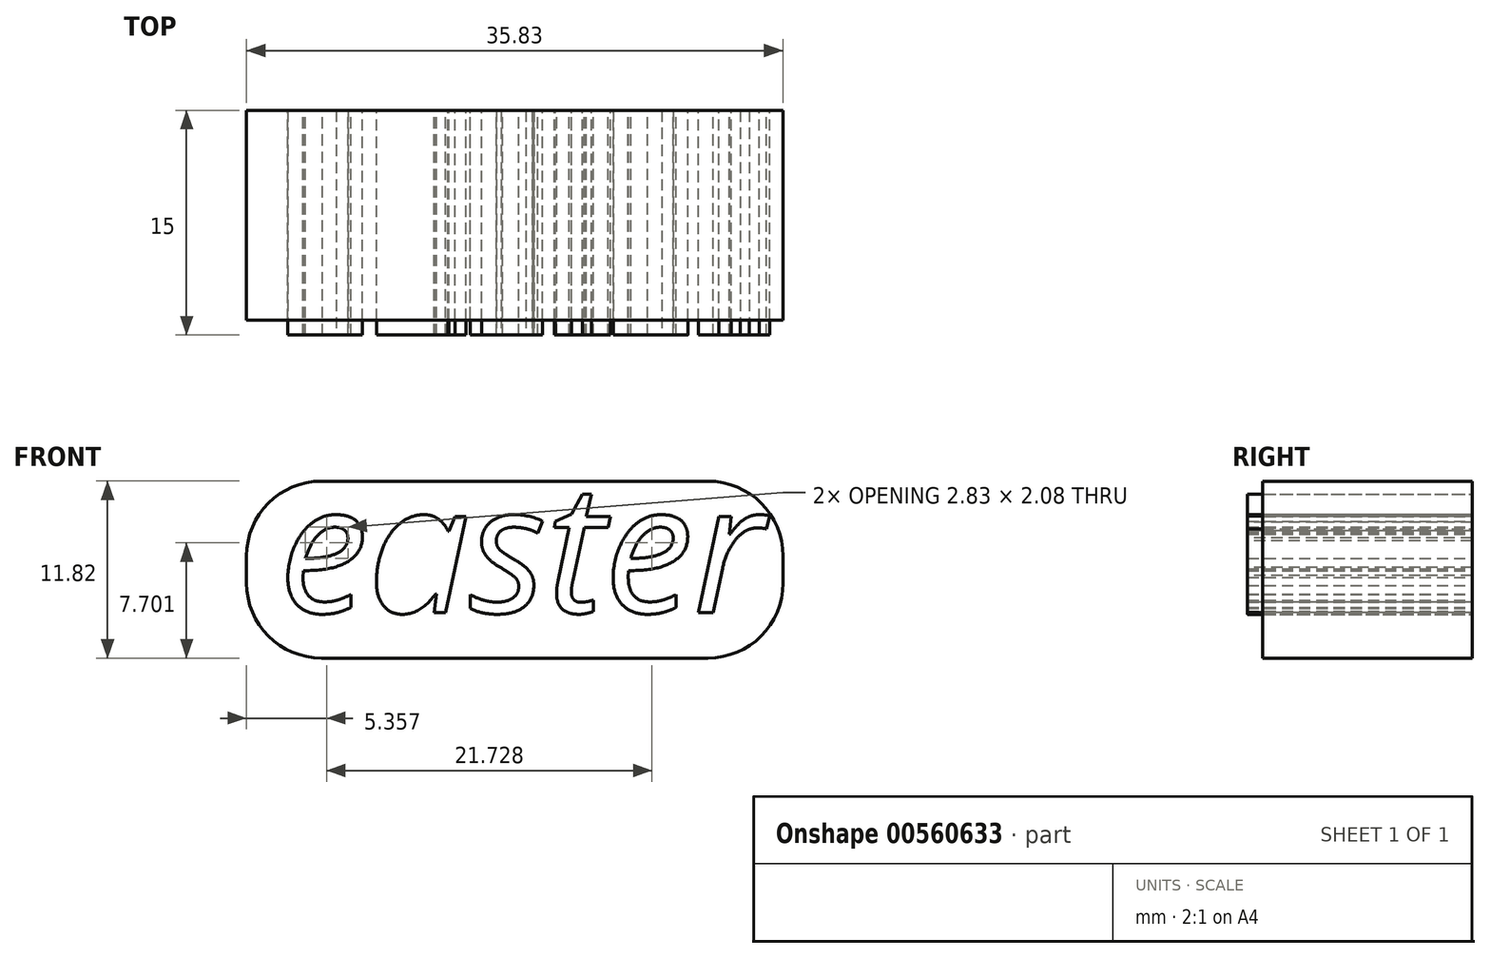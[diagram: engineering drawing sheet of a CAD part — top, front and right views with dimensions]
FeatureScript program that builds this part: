
annotation { "Feature Type Name" : "Feature", "Feature Type Description" : "" }
export const myFeature = defineFeature(function(context is Context, id is Id, definition is map)
    precondition{}
    {
        {
            var Q0;
            Q0=qCreatedBy(makeId("Front.planeOp"),FACE);
            var sketch = newSketch(context, id + "F0", { "sketchPlane" : qUnion([Q0])});
            skPoint(sketch, "E0.21.internal.orphan", {"position": v(0, -2.46) * mm});
            skPoint(sketch, "E0.22.internal.orphan", {"position": v(0, -2.08) * mm});
            skPoint(sketch, "E0.28.internal.orphan", {"position": v(-2.91, 0) * mm});
            skPoint(sketch, "E0.7.internal.orphan", {"position": v(0, 5.92) * mm});
            skText(sketch, "E1", { "text": "easter\n", "fontName": "OpenSans-Italic.ttf"});
            skLineSegment(sketch, "E2.bottom", {"start": v(-20.06, 30.88) * mm, "end": v(19.94, 30.88) * mm, "construction": true});
            skLineSegment(sketch, "E2.top", {"start": v(-20.06, -9.12) * mm, "end": v(19.94, -9.12) * mm, "construction": true});
            skLineSegment(sketch, "E2.left", {"start": v(-20.06, 30.88) * mm, "end": v(-20.06, -9.12) * mm, "construction": true});
            skLineSegment(sketch, "E2.right", {"start": v(19.94, 30.88) * mm, "end": v(19.94, -9.12) * mm, "construction": true});
            const initialGuessF0  = {"E1": [-0.0168, -0.00387, 1, 0, 0.00864]};
            skSetInitialGuess(sketch, initialGuessF0);
            skSolve(sketch);
        }
        {
            var Q0;
            Q0 = qSketchRegion(id + "F0", true);
            var Q1;
            Q1=makeQuery(id+"F0.imprint","IMPRINT",FACE,{"disambiguationData":[TD([[makeQuery(id+"F0.imprint","IMPRINT",EDGE,{"derivedFrom":sQuery(id+"F0.wireOp",EDGE,"E1.sketch_text.stroke-40")}),1.0]])]});
            extrude(context, id + "F1", {"entities" : qUnion([Q0, Q1]), "depth" : 15 * mm, "offsetDistance" : 25 * mm});
        }
        {
            var Q0;
            Q0=qCreatedBy(makeId("Front.planeOp"),FACE);
            var sketch = newSketch(context, id + "F2", { "sketchPlane" : qUnion([Q0])});
            skLineSegment(sketch, "E3.bottom", {"start": v(-13.99, 4.9) * mm, "end": v(11.84, 4.9) * mm});
            skLineSegment(sketch, "E3.top", {"start": v(-13.99, -6.9) * mm, "end": v(11.84, -6.9) * mm});
            skLineSegment(sketch, "E3.left", {"start": v(-18.99, -0.1) * mm, "end": v(-18.99, -1.9) * mm});
            skLineSegment(sketch, "E3.right", {"start": v(16.84, -0.1) * mm, "end": v(16.84, -1.9) * mm});
            skPoint(sketch, "E4.visualSharp", {"position": v(-18.99, 4.9) * mm});
            skPoint(sketch, "E5.visualSharp", {"position": v(16.84, 4.9) * mm});
            skPoint(sketch, "E6.visualSharp", {"position": v(16.84, -6.9) * mm});
            skPoint(sketch, "E7.visualSharp", {"position": v(-18.99, -6.9) * mm});
            skLineSegment(sketch, "E8", {"start": v(-18.99, -6.9) * mm, "end": v(-18.99, -8.23) * mm});
            skLineSegment(sketch, "E9", {"start": v(-17.4, -9.82) * mm, "end": v(-18.99, -6.9) * mm});
            skLineSegment(sketch, "E10", {"start": v(15.26, -9.82) * mm, "end": v(16.84, -6.9) * mm});
            skLineSegment(sketch, "E11", {"start": v(16.84, -6.9) * mm, "end": v(16.84, -8.23) * mm});
            skLineSegment(sketch, "E12", {"start": v(16.84, 3.33) * mm, "end": v(16.84, 4.9) * mm});
            skLineSegment(sketch, "E13", {"start": v(15.26, 4.9) * mm, "end": v(16.84, 4.9) * mm});
            skLineSegment(sketch, "E14", {"start": v(-18.99, 4.9) * mm, "end": v(-18.99, 3.33) * mm});
            skLineSegment(sketch, "E15", {"start": v(-17.4, 4.9) * mm, "end": v(-18.99, 4.9) * mm});
            skLineSegment(sketch, "E16.bottom", {"start": v(-20.68, 23.25) * mm, "end": v(19.32, 23.25) * mm, "construction": true});
            skLineSegment(sketch, "E16.top", {"start": v(-20.68, -16.75) * mm, "end": v(19.32, -16.75) * mm, "construction": true});
            skLineSegment(sketch, "E16.left", {"start": v(-20.68, 23.25) * mm, "end": v(-20.68, -16.75) * mm, "construction": true});
            skLineSegment(sketch, "E16.right", {"start": v(19.32, 23.25) * mm, "end": v(19.32, -16.75) * mm, "construction": true});
            skArc(sketch, "E17.filletArc", {"start": v(-13.99, 4.9) * mm, "mid": v(-17.52, 3.44) * mm, "end": v(-18.99, -0.1) * mm});
            skArc(sketch, "E18.filletArc", {"start": v(16.84, -0.1) * mm, "mid": v(15.38, 3.44) * mm, "end": v(11.84, 4.9) * mm});
            skArc(sketch, "E19.filletArc", {"start": v(11.84, -6.9) * mm, "mid": v(15.38, -5.44) * mm, "end": v(16.84, -1.9) * mm});
            skArc(sketch, "E20.filletArc", {"start": v(-18.99, -1.9) * mm, "mid": v(-17.52, -5.44) * mm, "end": v(-13.99, -6.9) * mm});
            skSolve(sketch);
        }
        {
            var Q0;
            Q0=makeQuery(id+"F2.imprint","IMPRINT",FACE,{"disambiguationData":[TD([[makeQuery(id+"F2.imprint","IMPRINT",EDGE,{"derivedFrom":sQuery(id+"F2.wireOp",EDGE,"E3.bottom")}),-1.0]])]});
            extrude(context, id + "F3", {"entities" : qUnion([Q0]), "depth" : 14 * mm, "offsetDistance" : 25 * mm});
        }
    });
